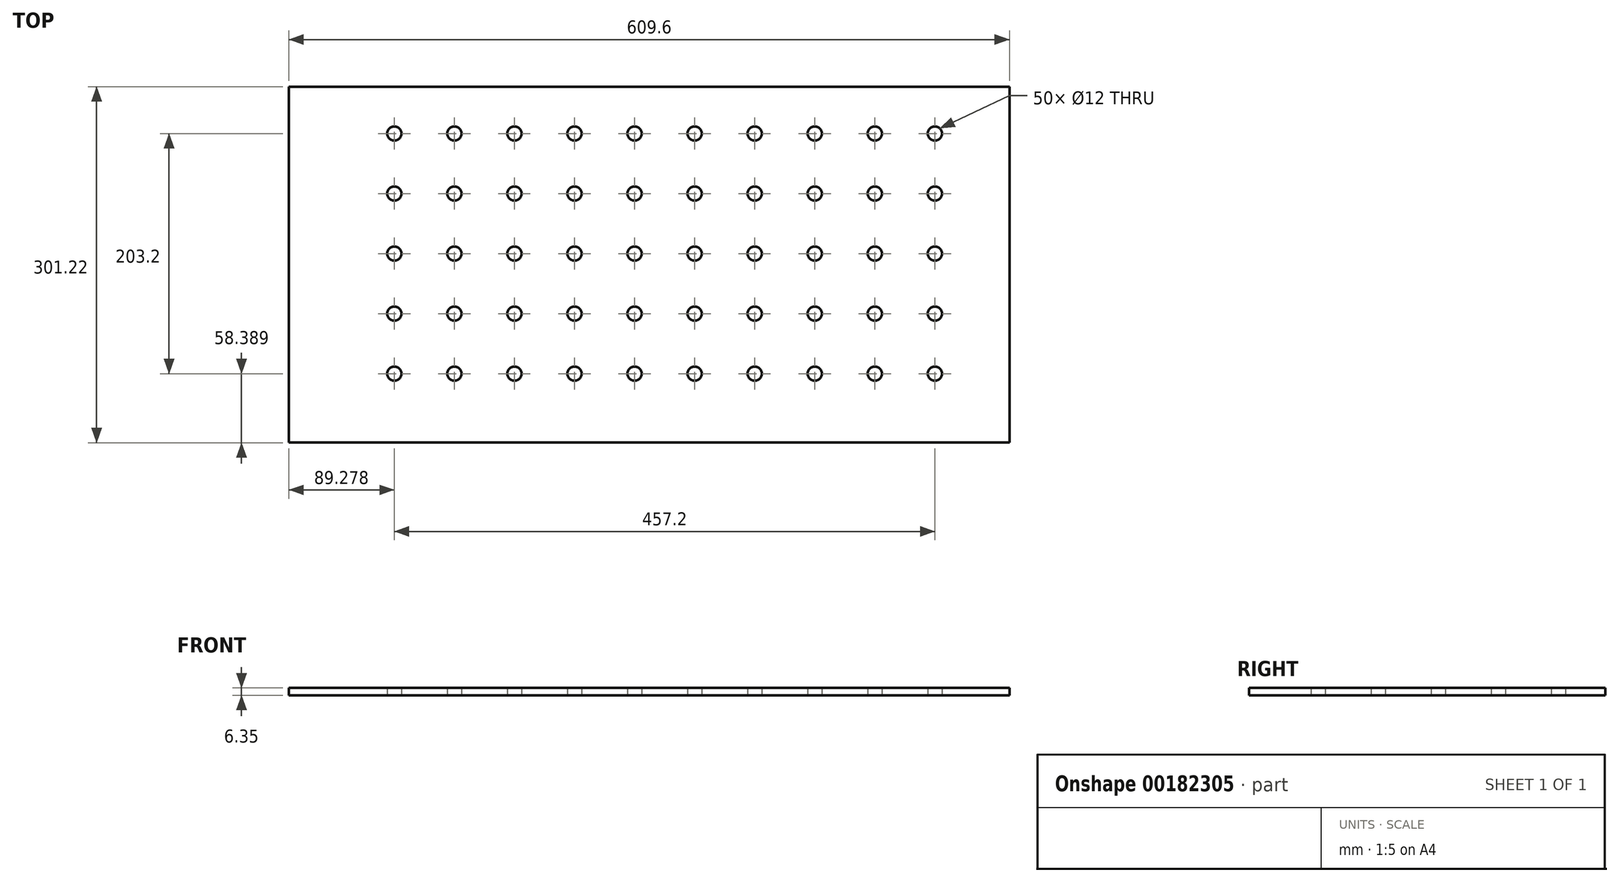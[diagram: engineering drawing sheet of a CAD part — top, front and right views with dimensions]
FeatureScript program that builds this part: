
annotation { "Feature Type Name" : "Feature", "Feature Type Description" : "" }
export const myFeature = defineFeature(function(context is Context, id is Id, definition is map)
    precondition{}
    {
        {
            var Q0;
            Q0=qCreatedBy(makeId("Top.planeOp"),FACE);
            var sketch = newSketch(context, id + "F0", { "sketchPlane" : qUnion([Q0])});
            skCircle(sketch, "E0", {"center": v(-166.02, 28.34) * mm, "radius": 6 * mm});
            skCircle(sketch, "E1.2.0.0", {"center": v(1053.18, 28.34) * mm, "radius": 6 * mm});
            skCircle(sketch, "E1.2.1.0", {"center": v(1053.18, 333.14) * mm, "radius": 6 * mm});
            skCircle(sketch, "E2.0.1.0", {"center": v(-166.02, 79.14) * mm, "radius": 6 * mm});
            skCircle(sketch, "E2.0.2.0", {"center": v(-166.02, 129.94) * mm, "radius": 6 * mm});
            skCircle(sketch, "E2.0.3.0", {"center": v(-166.02, 180.74) * mm, "radius": 6 * mm});
            skCircle(sketch, "E2.0.4.0", {"center": v(-166.02, 231.54) * mm, "radius": 6 * mm});
            skCircle(sketch, "E2.1.0.0", {"center": v(-115.22, 28.34) * mm, "radius": 6 * mm});
            skCircle(sketch, "E2.1.1.0", {"center": v(-115.22, 79.14) * mm, "radius": 6 * mm});
            skCircle(sketch, "E2.1.2.0", {"center": v(-115.22, 129.94) * mm, "radius": 6 * mm});
            skCircle(sketch, "E2.1.3.0", {"center": v(-115.22, 180.74) * mm, "radius": 6 * mm});
            skCircle(sketch, "E2.1.4.0", {"center": v(-115.22, 231.54) * mm, "radius": 6 * mm});
            skCircle(sketch, "E2.2.0.0", {"center": v(-64.42, 28.34) * mm, "radius": 6 * mm});
            skCircle(sketch, "E2.2.1.0", {"center": v(-64.42, 79.14) * mm, "radius": 6 * mm});
            skCircle(sketch, "E2.2.2.0", {"center": v(-64.42, 129.94) * mm, "radius": 6 * mm});
            skCircle(sketch, "E2.2.3.0", {"center": v(-64.42, 180.74) * mm, "radius": 6 * mm});
            skCircle(sketch, "E2.2.4.0", {"center": v(-64.42, 231.54) * mm, "radius": 6 * mm});
            skCircle(sketch, "E2.3.0.0", {"center": v(-13.62, 28.34) * mm, "radius": 6 * mm});
            skCircle(sketch, "E2.3.1.0", {"center": v(-13.62, 79.14) * mm, "radius": 6 * mm});
            skCircle(sketch, "E2.3.2.0", {"center": v(-13.62, 129.94) * mm, "radius": 6 * mm});
            skCircle(sketch, "E2.3.3.0", {"center": v(-13.62, 180.74) * mm, "radius": 6 * mm});
            skCircle(sketch, "E2.3.4.0", {"center": v(-13.62, 231.54) * mm, "radius": 6 * mm});
            skCircle(sketch, "E2.4.0.0", {"center": v(37.18, 28.34) * mm, "radius": 6 * mm});
            skCircle(sketch, "E2.4.1.0", {"center": v(37.18, 79.14) * mm, "radius": 6 * mm});
            skCircle(sketch, "E2.4.2.0", {"center": v(37.18, 129.94) * mm, "radius": 6 * mm});
            skCircle(sketch, "E2.4.3.0", {"center": v(37.18, 180.74) * mm, "radius": 6 * mm});
            skCircle(sketch, "E2.4.4.0", {"center": v(37.18, 231.54) * mm, "radius": 6 * mm});
            skCircle(sketch, "E2.5.0.0", {"center": v(87.98, 28.34) * mm, "radius": 6 * mm});
            skCircle(sketch, "E2.5.1.0", {"center": v(87.98, 79.14) * mm, "radius": 6 * mm});
            skCircle(sketch, "E2.5.2.0", {"center": v(87.98, 129.94) * mm, "radius": 6 * mm});
            skCircle(sketch, "E2.5.3.0", {"center": v(87.98, 180.74) * mm, "radius": 6 * mm});
            skCircle(sketch, "E2.5.4.0", {"center": v(87.98, 231.54) * mm, "radius": 6 * mm});
            skCircle(sketch, "E2.6.0.0", {"center": v(138.78, 28.34) * mm, "radius": 6 * mm});
            skCircle(sketch, "E2.6.1.0", {"center": v(138.78, 79.14) * mm, "radius": 6 * mm});
            skCircle(sketch, "E2.6.2.0", {"center": v(138.78, 129.94) * mm, "radius": 6 * mm});
            skCircle(sketch, "E2.6.3.0", {"center": v(138.78, 180.74) * mm, "radius": 6 * mm});
            skCircle(sketch, "E2.6.4.0", {"center": v(138.78, 231.54) * mm, "radius": 6 * mm});
            skCircle(sketch, "E2.7.0.0", {"center": v(189.58, 28.34) * mm, "radius": 6 * mm});
            skCircle(sketch, "E2.7.1.0", {"center": v(189.58, 79.14) * mm, "radius": 6 * mm});
            skCircle(sketch, "E2.7.2.0", {"center": v(189.58, 129.94) * mm, "radius": 6 * mm});
            skCircle(sketch, "E2.7.3.0", {"center": v(189.58, 180.74) * mm, "radius": 6 * mm});
            skCircle(sketch, "E2.7.4.0", {"center": v(189.58, 231.54) * mm, "radius": 6 * mm});
            skCircle(sketch, "E2.8.0.0", {"center": v(240.38, 28.34) * mm, "radius": 6 * mm});
            skCircle(sketch, "E2.8.1.0", {"center": v(240.38, 79.14) * mm, "radius": 6 * mm});
            skCircle(sketch, "E2.8.2.0", {"center": v(240.38, 129.94) * mm, "radius": 6 * mm});
            skCircle(sketch, "E2.8.3.0", {"center": v(240.38, 180.74) * mm, "radius": 6 * mm});
            skCircle(sketch, "E2.8.4.0", {"center": v(240.38, 231.54) * mm, "radius": 6 * mm});
            skCircle(sketch, "E2.9.0.0", {"center": v(291.18, 28.34) * mm, "radius": 6 * mm});
            skCircle(sketch, "E2.9.1.0", {"center": v(291.18, 79.14) * mm, "radius": 6 * mm});
            skCircle(sketch, "E2.9.2.0", {"center": v(291.18, 129.94) * mm, "radius": 6 * mm});
            skCircle(sketch, "E2.9.3.0", {"center": v(291.18, 180.74) * mm, "radius": 6 * mm});
            skCircle(sketch, "E2.9.4.0", {"center": v(291.18, 231.54) * mm, "radius": 6 * mm});
            skLineSegment(sketch, "E2.direction1", {"start": v(-166.02, 28.34) * mm, "end": v(-115.22, 28.34) * mm, "construction": true});
            skLineSegment(sketch, "E2.direction2", {"start": v(-166.02, 28.34) * mm, "end": v(-166.02, 79.14) * mm, "construction": true});
            skSolve(sketch);
        }
        {
            var Q0;
            Q0=qCreatedBy(makeId("Top.planeOp"),FACE);
            var sketch = newSketch(context, id + "F1", { "sketchPlane" : qUnion([Q0])});
            skLineSegment(sketch, "E3.bottom", {"start": v(-255.3, 271.17) * mm, "end": v(354.3, 271.17) * mm});
            skLineSegment(sketch, "E3.top", {"start": v(-255.3, -30.05) * mm, "end": v(354.3, -30.05) * mm});
            skLineSegment(sketch, "E3.left", {"start": v(-255.3, 271.17) * mm, "end": v(-255.3, -30.05) * mm});
            skLineSegment(sketch, "E3.right", {"start": v(354.3, 271.17) * mm, "end": v(354.3, -30.05) * mm});
            skSolve(sketch);
        }
        {
            var Q0;
            Q0=makeQuery(id+"F1.imprint","IMPRINT",FACE,{"disambiguationData":[TD([[makeQuery(id+"F1.imprint","IMPRINT",EDGE,{"derivedFrom":sQuery(id+"F1.wireOp",EDGE,"E3.bottom")}),-1.0]])]});
            extrude(context, id + "F2", {"entities" : qUnion([Q0]), "depth" : 6.35 * mm});
        }
        {
            var Q0;
            Q0=sQuery(id+"F0.wireOp",VERTEX,"E2.0.4.0.center");
            var Q1;
            Q1=sQuery(id+"F0.wireOp",VERTEX,"E2.0.3.0.center");
            var Q2;
            Q2=sQuery(id+"F0.wireOp",VERTEX,"E2.0.2.0.center");
            var Q3;
            Q3=sQuery(id+"F0.wireOp",VERTEX,"E2.0.1.0.center");
            var Q4;
            Q4=sQuery(id+"F0.wireOp",VERTEX,"E2.direction1.start");
            var Q5;
            Q5=sQuery(id+"F0.wireOp",VERTEX,"E2.5.2.0.center");
            var Q6;
            Q6=sQuery(id+"F0.wireOp",VERTEX,"E2.6.1.0.center");
            var Q7;
            Q7=sQuery(id+"F0.wireOp",VERTEX,"E2.3.0.0.center");
            var Q8;
            Q8=sQuery(id+"F0.wireOp",VERTEX,"E2.3.3.0.center");
            var Q9;
            Q9=sQuery(id+"F0.wireOp",VERTEX,"E2.4.4.0.center");
            var Q10;
            Q10=sQuery(id+"F0.wireOp",VERTEX,"E2.6.4.0.center");
            var Q11;
            Q11=sQuery(id+"F0.wireOp",VERTEX,"E2.2.1.0.center");
            var Q12;
            Q12=sQuery(id+"F0.wireOp",VERTEX,"E2.8.1.0.center");
            var Q13;
            Q13=sQuery(id+"F0.wireOp",VERTEX,"E2.7.3.0.center");
            var Q14;
            Q14=sQuery(id+"F0.wireOp",VERTEX,"E2.3.1.0.center");
            var Q15;
            Q15=sQuery(id+"F0.wireOp",VERTEX,"E2.5.3.0.center");
            var Q16;
            Q16=sQuery(id+"F0.wireOp",VERTEX,"E2.4.2.0.center");
            var Q17;
            Q17=sQuery(id+"F0.wireOp",VERTEX,"E2.5.0.0.center");
            var Q18;
            Q18=sQuery(id+"F0.wireOp",VERTEX,"E2.6.2.0.center");
            var Q19;
            Q19=sQuery(id+"F0.wireOp",VERTEX,"E2.2.2.0.center");
            var Q20;
            Q20=sQuery(id+"F0.wireOp",VERTEX,"E2.8.0.0.center");
            var Q21;
            Q21=sQuery(id+"F0.wireOp",VERTEX,"E2.3.2.0.center");
            var Q22;
            Q22=sQuery(id+"F0.wireOp",VERTEX,"E2.6.3.0.center");
            var Q23;
            Q23=sQuery(id+"F0.wireOp",VERTEX,"E2.4.1.0.center");
            var Q24;
            Q24=sQuery(id+"F0.wireOp",VERTEX,"E2.7.2.0.center");
            var Q25;
            Q25=sQuery(id+"F0.wireOp",VERTEX,"E2.1.1.0.center");
            var Q26;
            Q26=sQuery(id+"F0.wireOp",VERTEX,"E2.7.0.0.center");
            var Q27;
            Q27=sQuery(id+"F0.wireOp",VERTEX,"E2.2.0.0.center");
            var Q28;
            Q28=sQuery(id+"F0.wireOp",VERTEX,"E2.5.1.0.center");
            var Q29;
            Q29=sQuery(id+"F0.wireOp",VERTEX,"E2.8.2.0.center");
            var Q30;
            Q30=sQuery(id+"F0.wireOp",VERTEX,"E2.1.0.0.center");
            var Q31;
            Q31=sQuery(id+"F0.wireOp",VERTEX,"E2.2.4.0.center");
            var Q32;
            Q32=sQuery(id+"F0.wireOp",VERTEX,"E2.4.3.0.center");
            var Q33;
            Q33=sQuery(id+"F0.wireOp",VERTEX,"E2.6.0.0.center");
            var Q34;
            Q34=sQuery(id+"F0.wireOp",VERTEX,"E2.1.4.0.center");
            var Q35;
            Q35=sQuery(id+"F0.wireOp",VERTEX,"E2.1.3.0.center");
            var Q36;
            Q36=sQuery(id+"F0.wireOp",VERTEX,"E2.1.2.0.center");
            var Q37;
            Q37=sQuery(id+"F0.wireOp",VERTEX,"E2.4.0.0.center");
            var Q38;
            Q38=sQuery(id+"F0.wireOp",VERTEX,"E2.7.1.0.center");
            var Q39;
            Q39=sQuery(id+"F0.wireOp",VERTEX,"E2.5.4.0.center");
            var Q40;
            Q40=sQuery(id+"F0.wireOp",VERTEX,"E2.2.3.0.center");
            var Q41;
            Q41=sQuery(id+"F0.wireOp",VERTEX,"E2.9.0.0.center");
            var Q42;
            Q42=sQuery(id+"F0.wireOp",VERTEX,"E2.3.4.0.center");
            var Q43;
            Q43=sQuery(id+"F0.wireOp",VERTEX,"E2.8.4.0.center");
            var Q44;
            Q44=sQuery(id+"F0.wireOp",VERTEX,"E2.8.3.0.center");
            var Q45;
            Q45=sQuery(id+"F0.wireOp",VERTEX,"E2.9.2.0.center");
            var Q46;
            Q46=sQuery(id+"F0.wireOp",VERTEX,"E2.9.3.0.center");
            var Q47;
            Q47=sQuery(id+"F0.wireOp",VERTEX,"E2.9.4.0.center");
            var Q48;
            Q48=sQuery(id+"F0.wireOp",VERTEX,"E2.9.1.0.center");
            var Q49;
            Q49=sQuery(id+"F0.wireOp",VERTEX,"E2.7.4.0.center");
            var Q50;
            Q50=makeQuery(id+"F2.opExtrude","SWEPT_BODY",BODY,{"disambiguationData":[OSD([sQuery(id+"F1.wireOp",EDGE,"E3.bottom"),sQuery(id+"F1.wireOp",EDGE,"E3.top"),sQuery(id+"F1.wireOp",EDGE,"E3.left"),sQuery(id+"F1.wireOp",EDGE,"E3.right")])]});
            hole(context, id + "F3", {"style" : HoleStyle.SIMPLE, "endStyle" : HoleEndStyle.THROUGH, "oppositeDirection" : true, "holeDiameter" : 12 * mm, "locations" : qUnion([Q0, Q1, Q2, Q3, Q4, Q5, Q6, Q7, Q8, Q9, Q10, Q11, Q12, Q13, Q14, Q15, Q16, Q17, Q18, Q19, Q20, Q21, Q22, Q23, Q24, Q25, Q26, Q27, Q28, Q29, Q30, Q31, Q32, Q33, Q34, Q35, Q36, Q37, Q38, Q39, Q40, Q41, Q42, Q43, Q44, Q45, Q46, Q47, Q48, Q49]), "scope" : qUnion([Q50]), "isTappedThrough" : true});
        }
    });
